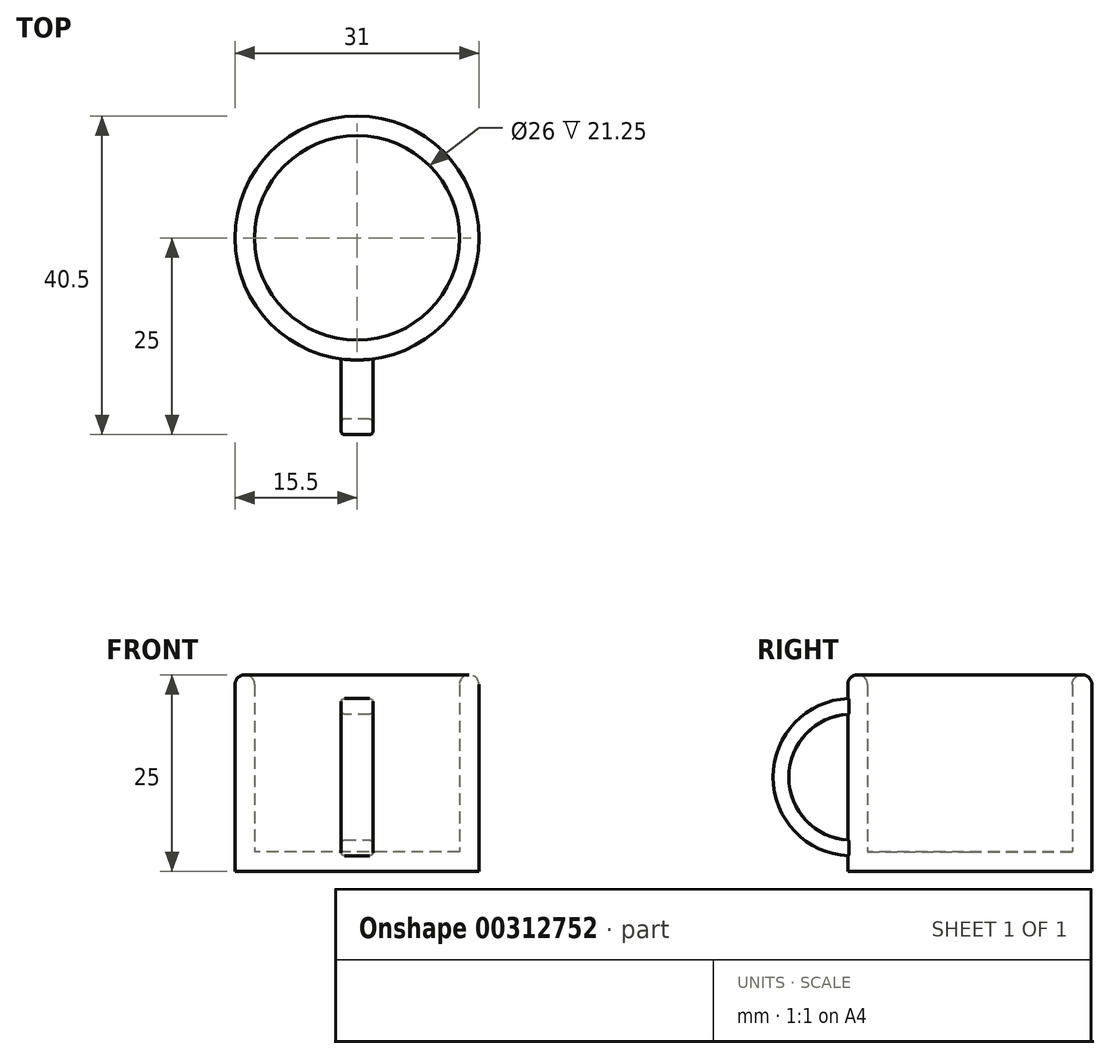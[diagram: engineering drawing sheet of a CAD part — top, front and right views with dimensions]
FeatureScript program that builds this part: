
annotation { "Feature Type Name" : "Feature", "Feature Type Description" : "" }
export const myFeature = defineFeature(function(context is Context, id is Id, definition is map)
    precondition{}
    {
        {
            var Q0;
            Q0=qCreatedBy(makeId("Top.planeOp"),FACE);
            var sketch = newSketch(context, id + "F0", { "sketchPlane" : qUnion([Q0])});
            skCircle(sketch, "E0", {"center": v(0, 0) * mm, "radius": 15.5 * mm});
            skSolve(sketch);
        }
        {
            var Q0;
            Q0=makeQuery(id+"F0.imprint","IMPRINT",FACE,{"disambiguationData":[TD([[makeQuery(id+"F0.imprint","IMPRINT",EDGE,{"derivedFrom":sQuery(id+"F0.wireOp",EDGE,"E0")}),1.0]])]});
            extrude(context, id + "F1", {"entities" : qUnion([Q0]), "depth" : 25 * mm});
        }
        {
            var Q0;
            Q0=makeQuery(id+"F1.opExtrude","CAP_FACE",FACE,{"disambiguationData":[OSD([sQuery(id+"F0.wireOp",EDGE,"E0")])],"isStart":false});
            shell(context, id + "F2", {"entities" : qUnion([Q0]), "thickness" : 2.5 * mm});
        }
        {
            var Q0;
            Q0=makeQuery(id+"F1.opExtrude","CAP_FACE",FACE,{"disambiguationData":[OSD([sQuery(id+"F0.wireOp",EDGE,"E0")])],"isStart":false});
            fillet(context, id + "F3", {"entities" : qUnion([Q0]), "radius" : 1.25 * mm, "tangentPropagation" : true, "allowEdgeOverflow" : false});
        }
        {
            var Q0;
            Q0=qCreatedBy(makeId("Front.planeOp"),FACE);
            cPlane(context, id + "F4", {"entities" : qUnion([Q0]), "cplaneType" : CPlaneType.OFFSET, "offset" : 15 * mm, "width" : 150 * mm, "height" : 150 * mm});
        }
        {
            var Q0;
            Q0=qCreatedBy(id+"F4.planeOp",FACE);
            var sketch = newSketch(context, id + "F5", { "sketchPlane" : qUnion([Q0])});
            skLineSegment(sketch, "E1.bottom", {"start": v(2, 20) * mm, "end": v(-2, 20) * mm});
            skLineSegment(sketch, "E1.top", {"start": v(2, 22) * mm, "end": v(-2, 22) * mm});
            skLineSegment(sketch, "E1.left", {"start": v(2, 20) * mm, "end": v(2, 22) * mm});
            skLineSegment(sketch, "E1.right", {"start": v(-2, 20) * mm, "end": v(-2, 22) * mm});
            skPoint(sketch, "E1.middle", {"position": v(0, 21) * mm});
            skLineSegment(sketch, "E2", {"start": v(0, 12) * mm, "end": v(2, 12) * mm});
            skSolve(sketch);
        }
        {
            var Q0;
            Q0=makeQuery(id+"F5.imprint","IMPRINT",FACE,{"disambiguationData":[TD([[makeQuery(id+"F5.imprint","IMPRINT",EDGE,{"derivedFrom":sQuery(id+"F5.wireOp",EDGE,"E1.bottom")}),-1.0]])]});
            var Q1;
            Q1=sQuery(id+"F5.wireOp",EDGE,"E2");
            revolve(context, id + "F6", {"operationType" : NewBodyOperationType.ADD, "entities" : qUnion([Q0]), "axis" : qUnion([Q1]), "revolveType" : RevolveType.ONE_DIRECTION, "angle" : 180 * degree});
        }
        {
            var Q0;
            Q0=makeQuery(id+"F6.opRevolve","SWEPT_EDGE",EDGE,{"disambiguationData":[OSD([sQuery(id+"F5.wireOp",EDGE,"E1.top"),sQuery(id+"F5.wireOp",EDGE,"E1.left")])]});
            var Q1;
            Q1=makeQuery(id+"F6.opRevolve","SWEPT_EDGE",EDGE,{"disambiguationData":[OSD([sQuery(id+"F5.wireOp",EDGE,"E1.top"),sQuery(id+"F5.wireOp",EDGE,"E1.right")])]});
            var Q2;
            Q2=makeQuery(id+"F6.opRevolve","SWEPT_EDGE",EDGE,{"disambiguationData":[OSD([sQuery(id+"F5.wireOp",EDGE,"E1.bottom"),sQuery(id+"F5.wireOp",EDGE,"E1.left")])]});
            var Q3;
            Q3=makeQuery(id+"F6.opRevolve","SWEPT_EDGE",EDGE,{"disambiguationData":[OSD([sQuery(id+"F5.wireOp",EDGE,"E1.bottom"),sQuery(id+"F5.wireOp",EDGE,"E1.right")])]});
            fillet(context, id + "F7", {"entities" : qUnion([Q0, Q1, Q2, Q3]), "radius" : 0.4 * mm, "tangentPropagation" : true, "allowEdgeOverflow" : false});
        }
    });
